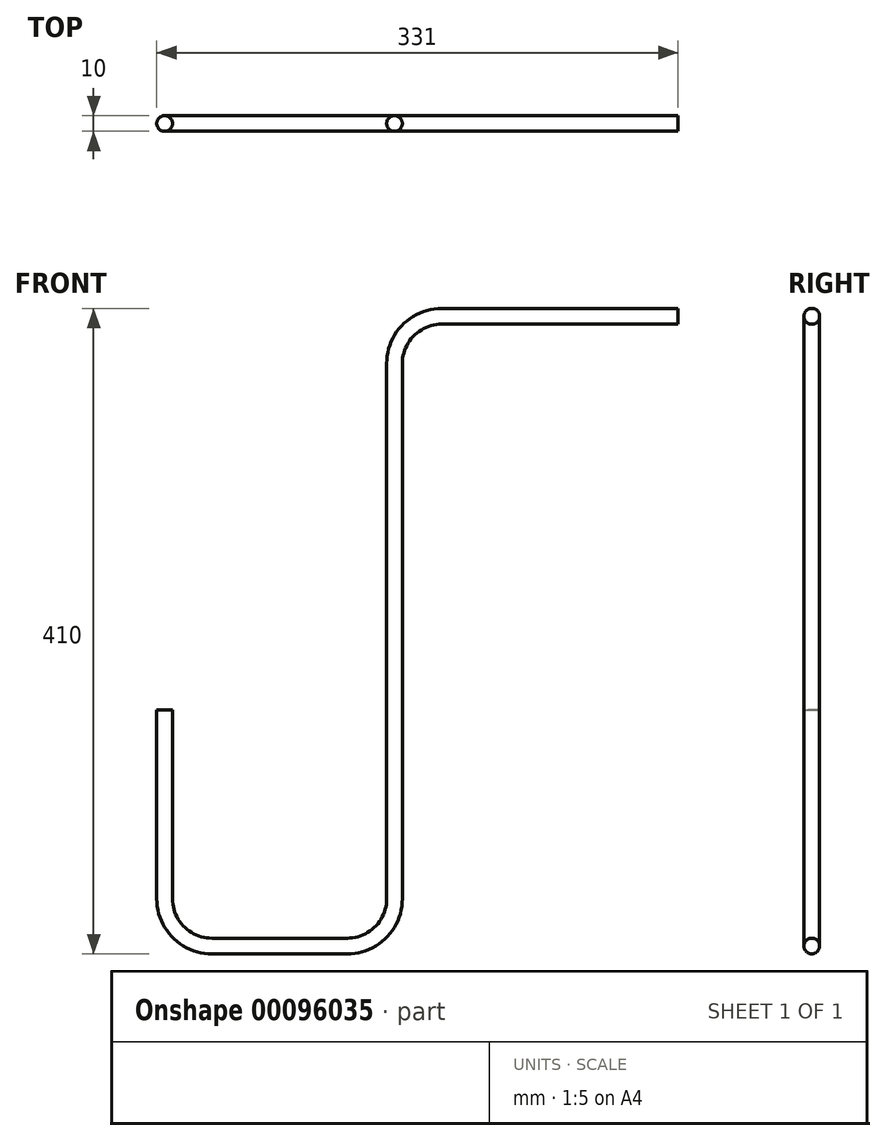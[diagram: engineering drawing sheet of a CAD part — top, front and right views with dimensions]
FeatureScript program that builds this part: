
annotation { "Feature Type Name" : "Feature", "Feature Type Description" : "" }
export const myFeature = defineFeature(function(context is Context, id is Id, definition is map)
    precondition{}
    {
        {
            var Q0;
            Q0=qCreatedBy(makeId("Front.planeOp"),FACE);
            var sketch = newSketch(context, id + "F0", { "sketchPlane" : qUnion([Q0])});
            skLineSegment(sketch, "E0", {"start": v(0, 0) * mm, "end": v(-150, 0) * mm});
            skLineSegment(sketch, "E1", {"start": v(-180, -30) * mm, "end": v(-180, -370) * mm});
            skLineSegment(sketch, "E2", {"start": v(-210, -400) * mm, "end": v(-296, -400) * mm});
            skLineSegment(sketch, "E3", {"start": v(-326, -370) * mm, "end": v(-326, -250) * mm});
            skPoint(sketch, "E4.visualSharp", {"position": v(-180, 0) * mm});
            skArc(sketch, "E4.filletArc", {"start": v(-150, 0) * mm, "mid": v(-171.21, -8.79) * mm, "end": v(-180, -30) * mm});
            skPoint(sketch, "E5.visualSharp", {"position": v(-180, -400) * mm});
            skArc(sketch, "E5.filletArc", {"start": v(-210, -400) * mm, "mid": v(-188.79, -391.21) * mm, "end": v(-180, -370) * mm});
            skPoint(sketch, "E6.visualSharp", {"position": v(-326, -400) * mm});
            skArc(sketch, "E6.filletArc", {"start": v(-326, -370) * mm, "mid": v(-317.21, -391.21) * mm, "end": v(-296, -400) * mm});
            skSolve(sketch);
        }
        {
            var Q0;
            Q0=qCreatedBy(makeId("Right.planeOp"),FACE);
            var sketch = newSketch(context, id + "F1", { "sketchPlane" : qUnion([Q0])});
            skCircle(sketch, "E7", {"center": v(0, 0) * mm, "radius": 5 * mm});
            skSolve(sketch);
        }
        {
            var Q0;
            Q0 = qSketchRegion(id + "F1", true);
            var Q1;
            Q1 = qConstructionFilter(qBodyType(qCreatedBy(id + "F0" ,EDGE), BodyType.WIRE), ConstructionObject.NO);
            sweep(context, id + "F2", {"profiles" : qUnion([Q0]), "path" : qUnion([Q1])});
        }
    });
